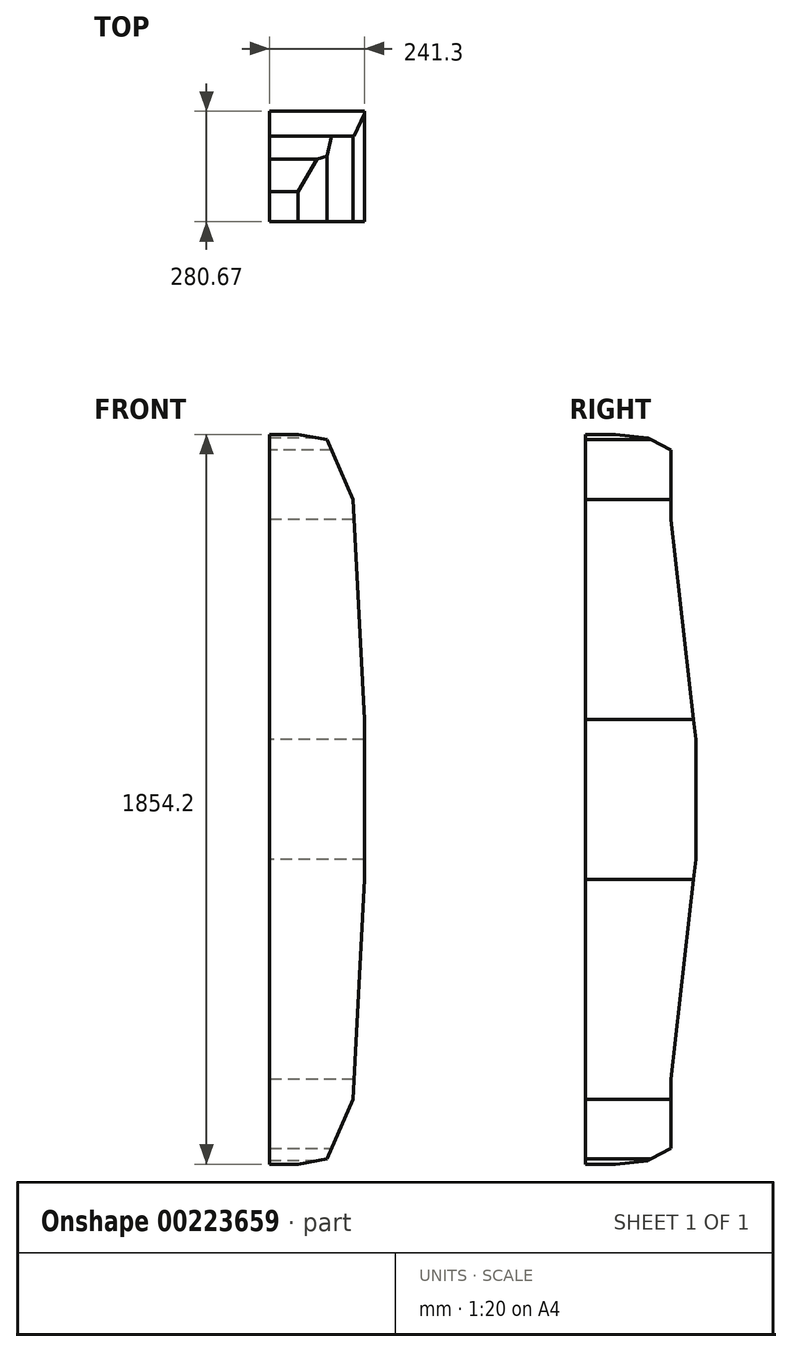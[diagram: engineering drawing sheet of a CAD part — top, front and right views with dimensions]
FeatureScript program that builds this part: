
annotation { "Feature Type Name" : "Feature", "Feature Type Description" : "" }
export const myFeature = defineFeature(function(context is Context, id is Id, definition is map)
    precondition{}
    {
        {
            var Q0;
            Q0=qCreatedBy(makeId("Top.planeOp"),FACE);
            var sketch = newSketch(context, id + "F0", { "sketchPlane" : qUnion([Q0])});
            skLineSegment(sketch, "E0.bottom", {"start": v(6527.8, -1778) * mm, "end": v(6223, -1778) * mm});
            skLineSegment(sketch, "E0.top", {"start": v(6527.8, -1422.4) * mm, "end": v(6223, -1422.4) * mm});
            skLineSegment(sketch, "E0.left", {"start": v(6527.8, -1778) * mm, "end": v(6527.8, -1422.4) * mm});
            skLineSegment(sketch, "E0.right", {"start": v(6223, -1778) * mm, "end": v(6223, -1422.4) * mm});
            skPoint(sketch, "E0.middle", {"position": v(6375.4, -1600.2) * mm});
            skSolve(sketch);
        }
        {
            var Q0;
            Q0=makeQuery(id+"F0.imprint","IMPRINT",FACE,{"disambiguationData":[TD([[makeQuery(id+"F0.imprint","IMPRINT",EDGE,{"derivedFrom":sQuery(id+"F0.wireOp",EDGE,"E0.bottom")}),-1.0]])]});
            extrude(context, id + "F1", {"entities" : qUnion([Q0]), "endBound" : BoundingType.SYMMETRIC, "depth" : 1905 * mm});
        }
        {
            var Q0;
            Q0=makeQuery(id+"F1.opExtrude","SWEPT_FACE",FACE,{"disambiguationData":[OSD([sQuery(id+"F0.wireOp",EDGE,"E0.bottom")])]});
            var sketch = newSketch(context, id + "F2", { "sketchPlane" : qUnion([Q0])});
            skLineSegment(sketch, "E1", {"start": v(6435.01, 762) * mm, "end": v(6464.3, 203.2) * mm});
            skLineSegment(sketch, "E2", {"start": v(6464.3, 203.2) * mm, "end": v(6464.3, 0) * mm});
            skPoint(sketch, "E2.endSnap0", {"position": v(6527.8, 0) * mm});
            skLineSegment(sketch, "E3", {"start": v(6527.8, 0) * mm, "end": v(6464.3, 0) * mm});
            skPoint(sketch, "E3.endSnap0", {"position": v(6223, 0) * mm});
            skLineSegment(sketch, "E4", {"start": v(6223, 1333.5) * mm, "end": v(8458.2, 1333.5) * mm});
            skLineSegment(sketch, "E5", {"start": v(8458.2, 1333.5) * mm, "end": v(8458.2, -1333.5) * mm});
            skLineSegment(sketch, "E6", {"start": v(6435.01, 762) * mm, "end": v(6369.22, 914.02) * mm});
            skLineSegment(sketch, "E7", {"start": v(6369.22, 914.02) * mm, "end": v(6223, 939.8) * mm});
            skLineSegment(sketch, "E8", {"start": v(6223, 939.8) * mm, "end": v(6223, 1333.5) * mm});
            skLineSegment(sketch, "E9.MirrorCS", {"start": v(6435.01, -762) * mm, "end": v(6464.3, -203.2) * mm});
            skLineSegment(sketch, "E10.MirrorCS", {"start": v(6223, -939.8) * mm, "end": v(6223, -1333.5) * mm});
            skLineSegment(sketch, "E11.MirrorCS", {"start": v(6435.01, -762) * mm, "end": v(6369.22, -914.02) * mm});
            skLineSegment(sketch, "E12.MirrorCS", {"start": v(6464.3, -203.2) * mm, "end": v(6464.3, 0) * mm});
            skLineSegment(sketch, "E13.MirrorCS", {"start": v(6369.22, -914.02) * mm, "end": v(6223, -939.8) * mm});
            skLineSegment(sketch, "E14", {"start": v(6223, -1333.5) * mm, "end": v(8458.2, -1333.5) * mm});
            skSolve(sketch);
        }
        {
            var Q0;
            Q0 = qSketchRegion(id + "F2", true);
            extrude(context, id + "F3", {"entities" : qUnion([Q0]), "operationType" : NewBodyOperationType.REMOVE, "endBound" : BoundingType.THROUGH_ALL, "oppositeDirection" : true, "depth" : 25.4 * mm});
        }
        {
            var Q0;
            Q0=makeQuery(id+"F1.opExtrude","SWEPT_FACE",FACE,{"disambiguationData":[OSD([sQuery(id+"F0.wireOp",EDGE,"E0.right")])]});
            var sketch = newSketch(context, id + "F4", { "sketchPlane" : qUnion([Q0])});
            skLineSegment(sketch, "E15.bottom", {"start": v(1741.17, 2238.7) * mm, "end": v(2316.61, 2238.7) * mm});
            skLineSegment(sketch, "E15.top", {"start": v(1741.17, -1932.79) * mm, "end": v(2316.61, -1932.79) * mm});
            skLineSegment(sketch, "E15.left", {"start": v(2316.61, 2238.7) * mm, "end": v(2316.61, -1932.79) * mm});
            skLineSegment(sketch, "E15.right", {"start": v(1741.17, 2238.7) * mm, "end": v(1741.17, -1932.79) * mm});
            skSolve(sketch);
        }
        {
            var Q0;
            Q0 = qSketchRegion(id + "F4", true);
            extrude(context, id + "F5", {"entities" : qUnion([Q0]), "operationType" : NewBodyOperationType.REMOVE, "endBound" : BoundingType.THROUGH_ALL, "oppositeDirection" : true, "depth" : 25.4 * mm});
        }
        {
            var Q0;
            Q0=makeQuery(id+"F1.opExtrude","SWEPT_FACE",FACE,{"disambiguationData":[OSD([sQuery(id+"F0.wireOp",EDGE,"E0.right")])]});
            var sketch = newSketch(context, id + "F6", { "sketchPlane" : qUnion([Q0])});
            skLineSegment(sketch, "E16", {"start": v(1460.5, 0) * mm, "end": v(1422.4, 0) * mm});
            skPoint(sketch, "E16.endSnap0", {"position": v(1422.4, 0) * mm});
            skLineSegment(sketch, "E17", {"start": v(1460.5, 0) * mm, "end": v(1460.5, -152.4) * mm});
            skLineSegment(sketch, "E18", {"start": v(1460.5, -152.4) * mm, "end": v(1524, -711.2) * mm});
            skLineSegment(sketch, "E19", {"start": v(1524, -711.2) * mm, "end": v(1524, -1382.62) * mm});
            skLineSegment(sketch, "E20.MirrorCS", {"start": v(1460.5, 0) * mm, "end": v(1460.5, 152.4) * mm});
            skLineSegment(sketch, "E21.MirrorCS", {"start": v(1460.5, 152.4) * mm, "end": v(1524, 711.2) * mm});
            skLineSegment(sketch, "E22.MirrorCS", {"start": v(1524, 711.2) * mm, "end": v(1524, 1382.62) * mm});
            skLineSegment(sketch, "E23", {"start": v(624.79, -1382.62) * mm, "end": v(1524, -1382.62) * mm});
            skLineSegment(sketch, "E24", {"start": v(624.79, -1382.62) * mm, "end": v(624.79, 1382.62) * mm});
            skLineSegment(sketch, "E25", {"start": v(624.79, 1382.62) * mm, "end": v(1524, 1382.62) * mm});
            skSolve(sketch);
        }
        {
            var Q0;
            {var subQ0=sQuery(id+"F6.wireOp",EDGE,"E23");Q0=makeQuery(id+"F6.imprint","IMPRINT",FACE,{"disambiguationData":[TD([[makeQuery(id+"F6.imprint","IMPRINT",EDGE,{"derivedFrom":subQ0}),1.0]])]});}
            var Q1;
            {var subQ5=sQuery(id+"F6.wireOp",EDGE,"E16");Q1=makeQuery(id+"F6.imprint","IMPRINT",FACE,{"disambiguationData":[TD([[makeQuery(id+"F6.imprint","IMPRINT",EDGE,{"derivedFrom":subQ5}),1.0]])]});}
            var Q2;
            {var subQ5=sQuery(id+"F6.wireOp",EDGE,"E16");Q2=makeQuery(id+"F6.imprint","IMPRINT",FACE,{"disambiguationData":[TD([[makeQuery(id+"F6.imprint","IMPRINT",EDGE,{"derivedFrom":subQ5}),-1.0]])]});}
            extrude(context, id + "F7", {"entities" : qUnion([Q0, Q1, Q2]), "operationType" : NewBodyOperationType.REMOVE, "endBound" : BoundingType.THROUGH_ALL, "oppositeDirection" : true, "depth" : 25.4 * mm});
        }
        {
            var Q0;
            Q0=makeQuery(id+"F1.opExtrude","SWEPT_FACE",FACE,{"disambiguationData":[OSD([sQuery(id+"F0.wireOp",EDGE,"E0.right")])]});
            var sketch = newSketch(context, id + "F8", { "sketchPlane" : qUnion([Q0])});
            skLineSegment(sketch, "E26", {"start": v(1741.17, 0) * mm, "end": v(2055.7, 0) * mm, "construction": true});
            skPoint(sketch, "E26.endSnap0", {"position": v(1741.17, 0) * mm});
            skLineSegment(sketch, "E27.MirrorCS", {"start": v(1407.1, 1074.56) * mm, "end": v(1753.9, 1074.56) * mm});
            skLineSegment(sketch, "E28.MirrorCS", {"start": v(1407.1, 825.2) * mm, "end": v(1407.1, 1074.56) * mm});
            skLineSegment(sketch, "E29.MirrorCS", {"start": v(1582.42, 918.42) * mm, "end": v(1407.1, 825.2) * mm});
            skLineSegment(sketch, "E30.MirrorCS", {"start": v(1664.97, 927.1) * mm, "end": v(1582.42, 918.42) * mm});
            skLineSegment(sketch, "E31", {"start": v(1753.9, 927.1) * mm, "end": v(1664.97, 927.1) * mm});
            skLineSegment(sketch, "E32", {"start": v(1753.9, 927.1) * mm, "end": v(1753.9, 1074.56) * mm});
            skPoint(sketch, "E33.orphan", {"position": v(1844.55, 1074.56) * mm});
            skLineSegment(sketch, "E34.MirrorCS", {"start": v(1753.9, -927.1) * mm, "end": v(1664.97, -927.1) * mm});
            skLineSegment(sketch, "E35.MirrorCS", {"start": v(1407.1, -1074.56) * mm, "end": v(1753.9, -1074.56) * mm});
            skLineSegment(sketch, "E36.MirrorCS", {"start": v(1407.1, -825.2) * mm, "end": v(1407.1, -1074.56) * mm});
            skLineSegment(sketch, "E37.MirrorCS", {"start": v(1582.42, -918.42) * mm, "end": v(1407.1, -825.2) * mm});
            skLineSegment(sketch, "E38.MirrorCS", {"start": v(1664.97, -927.1) * mm, "end": v(1582.42, -918.42) * mm});
            skPoint(sketch, "E39.MirrorP", {"position": v(1844.55, -1074.56) * mm});
            skLineSegment(sketch, "E40.MirrorCS", {"start": v(1753.9, -927.1) * mm, "end": v(1753.9, -1074.56) * mm});
            skSolve(sketch);
        }
        {
            var Q0;
            Q0 = qSketchRegion(id + "F8", true);
            extrude(context, id + "F9", {"entities" : qUnion([Q0]), "operationType" : NewBodyOperationType.REMOVE, "endBound" : BoundingType.THROUGH_ALL, "oppositeDirection" : true, "depth" : 25.4 * mm});
        }
    });
